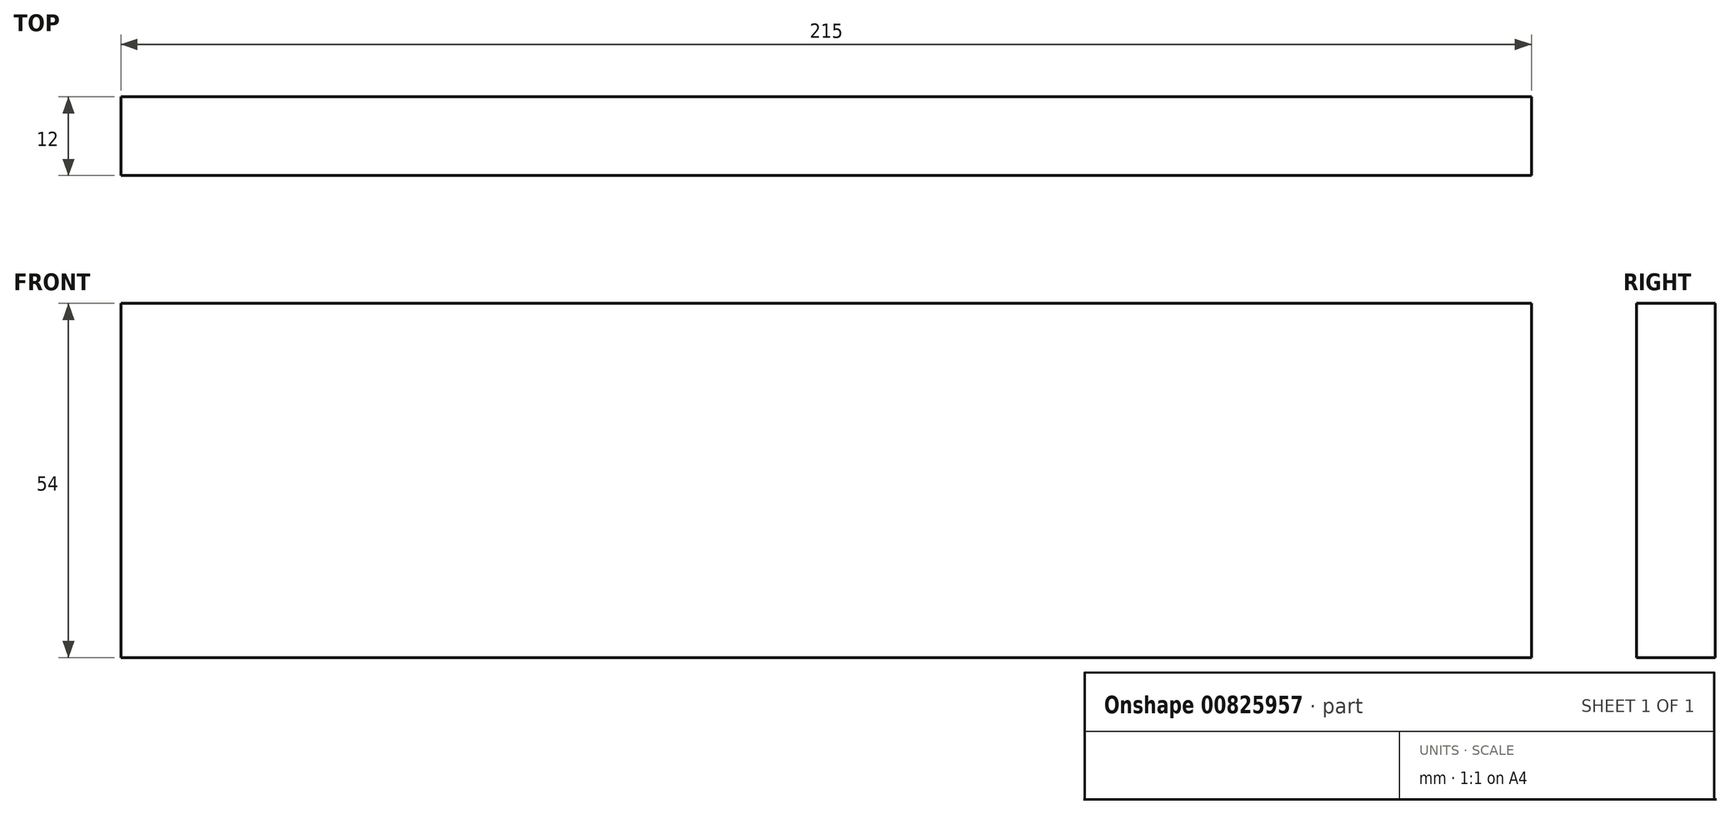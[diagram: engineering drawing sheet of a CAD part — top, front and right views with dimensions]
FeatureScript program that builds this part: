
annotation { "Feature Type Name" : "Feature", "Feature Type Description" : "" }
export const myFeature = defineFeature(function(context is Context, id is Id, definition is map)
    precondition{}
    {
        {
            var Q0;
            Q0=qCreatedBy(makeId("Front.planeOp"),FACE);
            var sketch = newSketch(context, id + "F0", { "sketchPlane" : qUnion([Q0])});
            skLineSegment(sketch, "E0.bottom", {"start": v(-107.5, 27) * mm, "end": v(107.5, 27) * mm});
            skLineSegment(sketch, "E0.top", {"start": v(-107.5, -27) * mm, "end": v(107.5, -27) * mm});
            skLineSegment(sketch, "E0.left", {"start": v(-107.5, 27) * mm, "end": v(-107.5, -27) * mm});
            skLineSegment(sketch, "E0.right", {"start": v(107.5, 27) * mm, "end": v(107.5, -27) * mm});
            skPoint(sketch, "E0.middle", {"position": v(0, 0) * mm});
            skSolve(sketch);
        }
        {
            var Q0;
            Q0 = qSketchRegion(id + "F0", true);
            extrude(context, id + "F1", {"entities" : qUnion([Q0]), "depth" : 12 * mm, "offsetDistance" : 25.4 * mm});
        }
    });
